# Revit family: LAMP_LUP DOWNLIGHT 162
name_source: partatom
category: Luminarias
revit_build: Autodesk Revit 2018 (Build: 20190510_1515(x64)
units: mm (PartAtom-declared; Revit-internal decimal feet)

## family parameters
Anfitrión = Cara
Compartido = No
Corte con vacíos al cargar = No
Cota de conector redondo = Diámetro de uso
Origen de luz = Sí
Punto de cálculo de habitación = No
Tipo de pieza = Normal

## types (4) — shared parameters
CRI = 80
Cambio de temperatura de color de luz atenuada = <Ninguno>
Diameter = 162 mm  [stored 0.531496 ft]
Elevación por defecto = 1219 mm
Filtro de color = 16777215
Finish = Texturised black RAL 9011
Gear = Electronic
Height = 195 mm  [stored 0.639764 ft]
Installation instructions = https://www.lamp.es
Insulation class = I
LED Lifetime = 50.000 L80 B10
Lamp = COB LED
Last update = 15/02/2022
MacAdam = 3
Manufacturer URL = http://www.lamp.es
Manufacturer country = Spain
Manufacturer name = LAMP
Material COB = LAMP_COB
Material cristal = LAMP_Cristal Bazz Transparente
Material cuerpo = LAMP_Aluminio Ocult Pendular NG
Material reflector = LAMP_Aluminio Reflector Imag
Power Supply = 220-240V 50/60Hz
Product URL = https://www.lamp.es
Product datasheet = http://www.lamp.es
Protection rating = IP65 / IK06
Type = COB PHILIPS
Weight = 2.53 kg
Ángulo de inclinación = -90.00°

## per-type parameters (varying)
| type | Archivo de red fotométrica | Efficacy | Plum | Power | Product code |
| 2162LM 4000 FLOOD BLACK | LS116230FL40NB.IES | 82 lm/W | 26 W | 23 W | LS116230FL40NB |
| 2392LM 4000 WIDE FLOOD BLACK | LS116230WF40NB.IES | 91 lm/W | 26 W | 23 W | LS116230WF40NB |
| 2850LM 4000 FLOOD BLACK | LS116240FL40NB.IES | 84 lm/W | 34 W | 30 W | LS116240FL40NB |
| 3114LM 4000 WIDE FLOOD BLACK | LS116240WF40NB.IES | 92 lm/W | 34 W | 30 W | LS116240WF40NB |

note: [stored X ft] marks values corroborated as IEEE doubles in the binary element streams (Revit-internal decimal feet)
